# Revit family: HVAC_Heat-Pump_Enertech_CTC_CombiAir-16M
name_source: partatom
category: Specialty Equipment
revit_build: Autodesk Revit 2018 (Build: 20170223_1515(x64)
units: mm (PartAtom-declared; Revit-internal decimal feet)

## family parameters
Always vertical = Yes
Cut with Voids When Loaded = No
OmniClass Number = 23.75.00.00
OmniClass Title = Climate Control (HVAC)
Part Type = Normal
Room Calculation Point = No
Round Connector Dimension = Use Diameter
Shared = No
Work Plane-Based = No

## types (1)
- CTC CombiAir 16M
    AirFlow = 6000 m3/h
    AssetType = Fixed
    BIMObjectName = HVAC_Heat-Pump_Enertech_CTC_CombiAir-16M
    Brand = CTC
    CO2Equivalent = 8.350 tonnes
    COP = 4.85
    Capacity = Variable
    Category = Heat Pumps, Air-to-water
    Color = grey
    Cooling capacity A35: W7/W18 = 13.04/15.70
    CoolingCapacity A27: W7/W18 = 13.30/17.70
    Cost = 0 $
    Description = CTC CombiAir 16M, a series of speed-controlled air-to-water heat pumps that adapt to the building’s power demand during the year. For the perfect indoor climate they produce both cooling and heating
    DurationUnit = Year
    EANNumber = 7333077093280
    EER A27: W7/W18 = 3.33/3.91
    EER A35: W7/W18 = 2.88/3.12
    ElectricalDeviceNominalPower = 0 W
    EnergyClassHeatingWithControl = A+++ / A++
    EnergyClassHeatingWithoutControl = A+++ / A++
    EnergyClass_HotWater_TapProfile = A/ L
    GroupFuse = 25 A
    HasProtectiveEarth = Yes
    IP_Code = IP 24
    IfcExportAs = IfcElectricalDeviceCommon
    IfcExportType = HEATER
    InPutPower = 1.45 kW
    Manufacturer = Enertech AB
    ManufacturerCountry = Sweden
    ManufacturerName = Enertech AB
    ManufacturerURL = https://ctc.se
    Material = Steel
    MaxOperatingPressureThermalStore = 4.5 bar
    MaxStartingCurrent = 5 A
    Model = CTC CombiAir 16M
    ModelNumber = 589353001
    NBSDescription = Air to water heat pumps
    NBSReference = 90-40-40/320
    Name = CTC_CombiAir-16M
    NominalCurrent = 0 A
    NominalDepth = 456 mm
    NominalFrequencyRange = 50 Hz
    NominalHeight = 1450 mm
    NominalVoltage = 230 V
    NominalWidth = 1144 mm
    NumberOfPoles = 1
    OutputRange = No data
    PhaseAngle = 0.00°
    ProductInformation = CTC CombiAir 16M, a series of speed-controlled air-to-water heat pumps that adapt to the building’s power demand during the year. For the perfect indoor climate they produce both cooling and heating
    PumpMainMaterial = Stainless Steel
    PumpSecondaryMaterial = Brass
    RatedCurrent = 25 A
    RatedHeatOutputModerate = 15 kW
    RatedVoltage = 230 V
    RefrigerantQuantity = 4.00 kg
    RefrigerantType = R410A
    SCOPCold = 3.48
    SCOPModerate = 4.48
    SCOPWarm = 5.99
    Shape = Rectangular
    Size = 452x1145x1450 mm
    Sound pressureLPA 10m = 36 dB
    Sound pressureLPA 5m = 42 dB
    SoundPowerLWA = 61 dB
    SpecifiedOutput = 15 kW
    Touchscreen = no
    UNSPSCCode = 40101806
    URL = https://ctc-heating.com
    Uniclass2 = Pr_40_70_65
    Uniclass2015Description = Preparation catering equipment
    Uniclass2015Reference = Pr_40_70_65
    UsageCurrent = 0 A
    Version = 1
    VersionDate = 24/05/2022
    WarrantyDurationUnit = Year
    WaterVolumeHeathingSystem = No data
    Weight = 144 kg

## geometry (parser evidence)
native form markers: Sweep x4
no freeform markers — native parametric forms only
